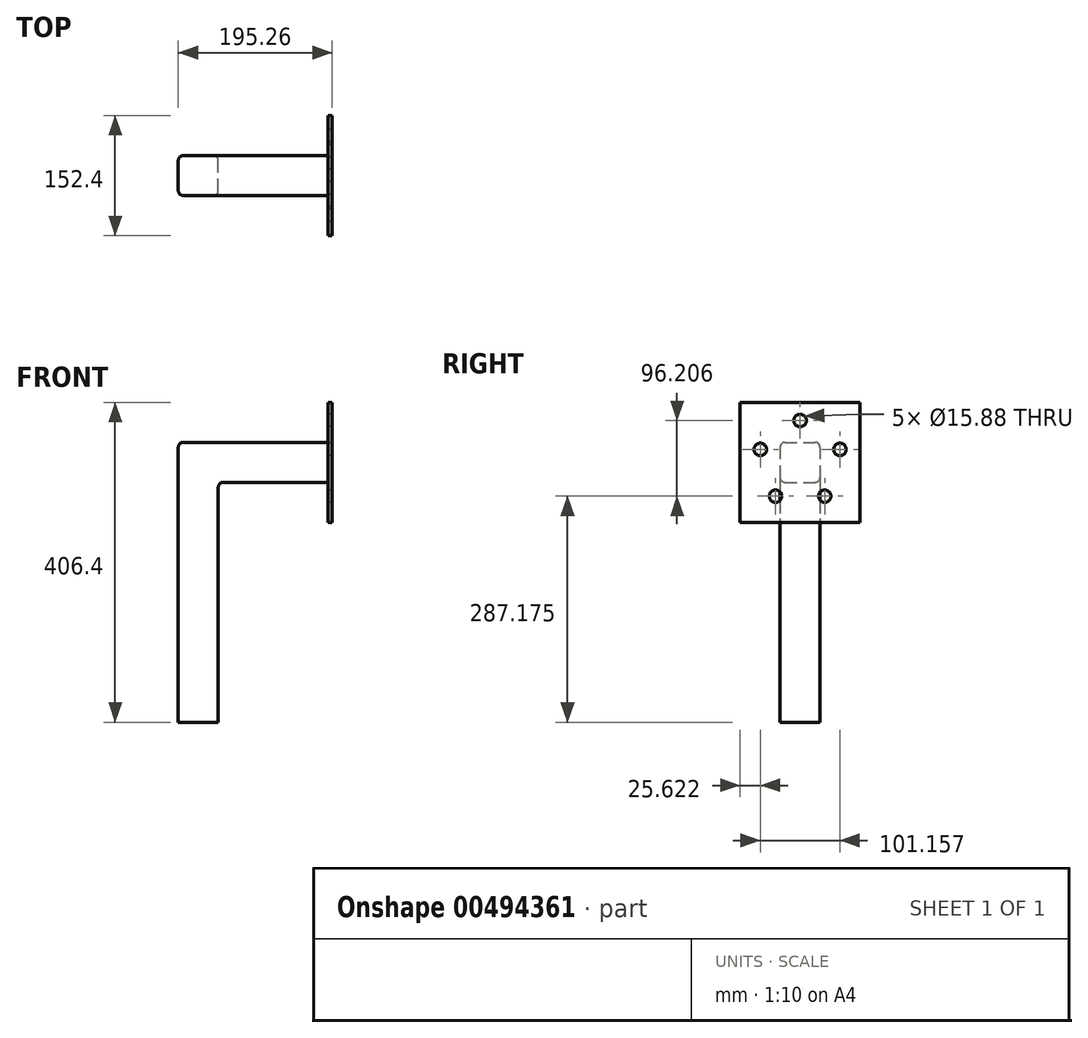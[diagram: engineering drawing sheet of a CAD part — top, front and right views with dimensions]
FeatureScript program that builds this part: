
annotation { "Feature Type Name" : "Feature", "Feature Type Description" : "" }
export const myFeature = defineFeature(function(context is Context, id is Id, definition is map)
    precondition{}
    {
        {
            var Q0;
            Q0=qCreatedBy(makeId("Front.planeOp"),FACE);
            var sketch = newSketch(context, id + "F0", { "sketchPlane" : qUnion([Q0])});
            skLineSegment(sketch, "E0.bottom", {"start": v(-24.27, 286.3) * mm, "end": v(26.53, 286.3) * mm});
            skLineSegment(sketch, "E0.top", {"start": v(-24.27, -69.3) * mm, "end": v(26.53, -69.3) * mm});
            skLineSegment(sketch, "E0.left", {"start": v(-24.27, 286.3) * mm, "end": v(-24.27, -69.3) * mm});
            skLineSegment(sketch, "E0.right", {"start": v(26.53, 235.5) * mm, "end": v(26.53, -69.3) * mm});
            skLineSegment(sketch, "E1.bottom", {"start": v(-24.27, 286.3) * mm, "end": v(166.23, 286.3) * mm});
            skLineSegment(sketch, "E1.top", {"start": v(26.53, 235.5) * mm, "end": v(166.23, 235.5) * mm});
            skLineSegment(sketch, "E1.left", {"start": v(-24.27, 286.3) * mm, "end": v(-24.27, 235.5) * mm});
            skLineSegment(sketch, "E1.right", {"start": v(166.23, 286.3) * mm, "end": v(166.23, 235.5) * mm});
            skLineSegment(sketch, "E2", {"start": v(-24.27, 286.3) * mm, "end": v(26.53, 235.5) * mm});
            skLineSegment(sketch, "E3.bottom", {"start": v(166.23, 337.1) * mm, "end": v(171, 337.1) * mm});
            skLineSegment(sketch, "E3.top", {"start": v(166.23, 184.7) * mm, "end": v(171, 184.7) * mm});
            skLineSegment(sketch, "E3.left", {"start": v(166.23, 337.1) * mm, "end": v(166.23, 184.7) * mm});
            skLineSegment(sketch, "E3.right", {"start": v(171, 337.1) * mm, "end": v(171, 184.7) * mm});
            skPoint(sketch, "E4.end.orphan", {"position": v(166.23, 260.9) * mm});
            skPoint(sketch, "E4.start.orphan", {"position": v(166.23, 260.9) * mm});
            skSolve(sketch);
        }
        {
            var Q0;
            Q0=makeQuery(id+"F0.imprint","IMPRINT",FACE,{"disambiguationData":[TD([[makeQuery(id+"F0.imprint","IMPRINT",EDGE,{"derivedFrom":sQuery(id+"F0.wireOp",EDGE,"E0.top")}),1.0]])]});
            var Q1;
            {var subQ4=sQuery(id+"F0.wireOp",EDGE,"E1.top");Q1=makeQuery(id+"F0.imprint","IMPRINT",FACE,{"disambiguationData":[TD([[makeQuery(id+"F0.imprint","IMPRINT",EDGE,{"derivedFrom":subQ4}),1.0]])]});}
            extrude(context, id + "F1", {"entities" : qUnion([Q0, Q1]), "endBound" : BoundingType.SYMMETRIC, "depth" : 50.8 * mm});
        }
        {
            var Q0;
            {var subQ3=sQuery(id+"F0.wireOp",EDGE,"E3.bottom");Q0=makeQuery(id+"F0.imprint","IMPRINT",FACE,{"disambiguationData":[TD([[makeQuery(id+"F0.imprint","IMPRINT",EDGE,{"derivedFrom":subQ3}),-1.0]])]});}
            extrude(context, id + "F2", {"entities" : qUnion([Q0]), "operationType" : NewBodyOperationType.ADD, "endBound" : BoundingType.SYMMETRIC, "depth" : 152.4 * mm});
        }
        {
            var Q0;
            Q0=makeQuery(id+"F2.opExtrude","SWEPT_FACE",FACE,{"disambiguationData":[OSD([sQuery(id+"F0.wireOp",EDGE,"E3.right")])]});
            cPlane(context, id + "F3", {"entities" : qUnion([Q0]), "cplaneType" : CPlaneType.OFFSET, "offset" : 0 * mm, "width" : 152.4 * mm, "height" : 152.4 * mm});
        }
        {
            var Q0;
            Q0=qCreatedBy(id+"F3.planeOp",FACE);
            var sketch = newSketch(context, id + "F4", { "sketchPlane" : qUnion([Q0])});
            skCircle(sketch, "E5", {"center": v(0, 260.9) * mm, "radius": 30.96 * mm});
            skCircle(sketch, "E6", {"center": v(0, 314.1) * mm, "radius": 7.94 * mm});
            skCircle(sketch, "E7.1.0", {"center": v(-50.58, 277.34) * mm, "radius": 7.94 * mm});
            skCircle(sketch, "E7.2.0", {"center": v(-31.26, 217.88) * mm, "radius": 7.94 * mm});
            skCircle(sketch, "E7.3.0", {"center": v(31.26, 217.88) * mm, "radius": 7.94 * mm});
            skCircle(sketch, "E7.4.0", {"center": v(50.58, 277.34) * mm, "radius": 7.94 * mm});
            skSolve(sketch);
        }
        {
            var Q0;
            Q0=makeQuery(id+"F4.imprint","IMPRINT",FACE,{"disambiguationData":[TD([[makeQuery(id+"F4.imprint","IMPRINT",EDGE,{"derivedFrom":sQuery(id+"F4.wireOp",EDGE,"E6")}),1.0]])]});
            var Q1;
            Q1=makeQuery(id+"F4.imprint","IMPRINT",FACE,{"disambiguationData":[TD([[makeQuery(id+"F4.imprint","IMPRINT",EDGE,{"derivedFrom":sQuery(id+"F4.wireOp",EDGE,"E7.1.0")}),1.0]])]});
            var Q2;
            Q2=makeQuery(id+"F4.imprint","IMPRINT",FACE,{"disambiguationData":[TD([[makeQuery(id+"F4.imprint","IMPRINT",EDGE,{"derivedFrom":sQuery(id+"F4.wireOp",EDGE,"E7.2.0")}),1.0]])]});
            var Q3;
            Q3=makeQuery(id+"F4.imprint","IMPRINT",FACE,{"disambiguationData":[TD([[makeQuery(id+"F4.imprint","IMPRINT",EDGE,{"derivedFrom":sQuery(id+"F4.wireOp",EDGE,"E7.3.0")}),1.0]])]});
            var Q4;
            Q4=makeQuery(id+"F4.imprint","IMPRINT",FACE,{"disambiguationData":[TD([[makeQuery(id+"F4.imprint","IMPRINT",EDGE,{"derivedFrom":sQuery(id+"F4.wireOp",EDGE,"E7.4.0")}),1.0]])]});
            var Q5;
            Q5=sQuery(id+"F4.wireOp",EDGE,"E6");
            var Q6;
            Q6=sQuery(id+"F4.wireOp",EDGE,"E7.1.0");
            var Q7;
            Q7=sQuery(id+"F4.wireOp",EDGE,"E7.2.0");
            var Q8;
            Q8=sQuery(id+"F4.wireOp",EDGE,"E7.3.0");
            var Q9;
            Q9=sQuery(id+"F4.wireOp",EDGE,"E7.4.0");
            extrude(context, id + "F5", {"entities" : qUnion([Q0, Q1, Q2, Q3, Q4]), "operationType" : NewBodyOperationType.REMOVE, "surfaceEntities" : qUnion([Q5, Q6, Q7, Q8, Q9]), "endBound" : BoundingType.SYMMETRIC, "depth" : 25.4 * mm});
        }
        {
            var Q0;
            Q0=makeQuery(id+"F1.opExtrude","CAP_EDGE",EDGE,{"disambiguationData":[OSD([sQuery(id+"F0.wireOp",EDGE,"E1.bottom")])],"isStart":false});
            var Q1;
            Q1=makeQuery(id+"F1.opExtrude","CAP_EDGE",EDGE,{"disambiguationData":[OSD([sQuery(id+"F0.wireOp",EDGE,"E1.bottom")])],"isStart":true});
            var Q2;
            Q2=makeQuery(id+"F1.opExtrude","SWEPT_EDGE",EDGE,{"disambiguationData":[OSD([sQuery(id+"F0.wireOp",EDGE,"E1.bottom"),sQuery(id+"F0.wireOp",EDGE,"E1.left"),sQuery(id+"F0.wireOp",EDGE,"E2")])]});
            var Q3;
            Q3=makeQuery(id+"F1.opExtrude","CAP_EDGE",EDGE,{"disambiguationData":[OSD([sQuery(id+"F0.wireOp",EDGE,"E0.left"),sQuery(id+"F0.wireOp",EDGE,"E1.left")])],"isStart":false});
            var Q4;
            Q4=makeQuery(id+"F1.opExtrude","CAP_EDGE",EDGE,{"disambiguationData":[OSD([sQuery(id+"F0.wireOp",EDGE,"E0.right")])],"isStart":false});
            var Q5;
            Q5=makeQuery(id+"F1.opExtrude","CAP_EDGE",EDGE,{"disambiguationData":[OSD([sQuery(id+"F0.wireOp",EDGE,"E0.right")])],"isStart":true});
            var Q6;
            Q6=makeQuery(id+"F1.opExtrude","CAP_EDGE",EDGE,{"disambiguationData":[OSD([sQuery(id+"F0.wireOp",EDGE,"E0.left"),sQuery(id+"F0.wireOp",EDGE,"E1.left")])],"isStart":true});
            fillet(context, id + "F6", {"entities" : qUnion([Q0, Q1, Q2, Q3, Q4, Q5, Q6]), "radius" : 6.35 * mm, "tangentPropagation" : true, "allowEdgeOverflow" : false});
        }
        {
            var Q0;
            Q0=makeQuery(id+"F1.opExtrude","CAP_EDGE",EDGE,{"disambiguationData":[OSD([sQuery(id+"F0.wireOp",EDGE,"E1.top")])],"isStart":false});
            var Q1;
            Q1=makeQuery(id+"F1.opExtrude","CAP_EDGE",EDGE,{"disambiguationData":[OSD([sQuery(id+"F0.wireOp",EDGE,"E1.top")])],"isStart":true});
            fillet(context, id + "F7", {"entities" : qUnion([Q0, Q1]), "radius" : 6.35 * mm, "tangentPropagation" : true, "allowEdgeOverflow" : false});
        }
    });
